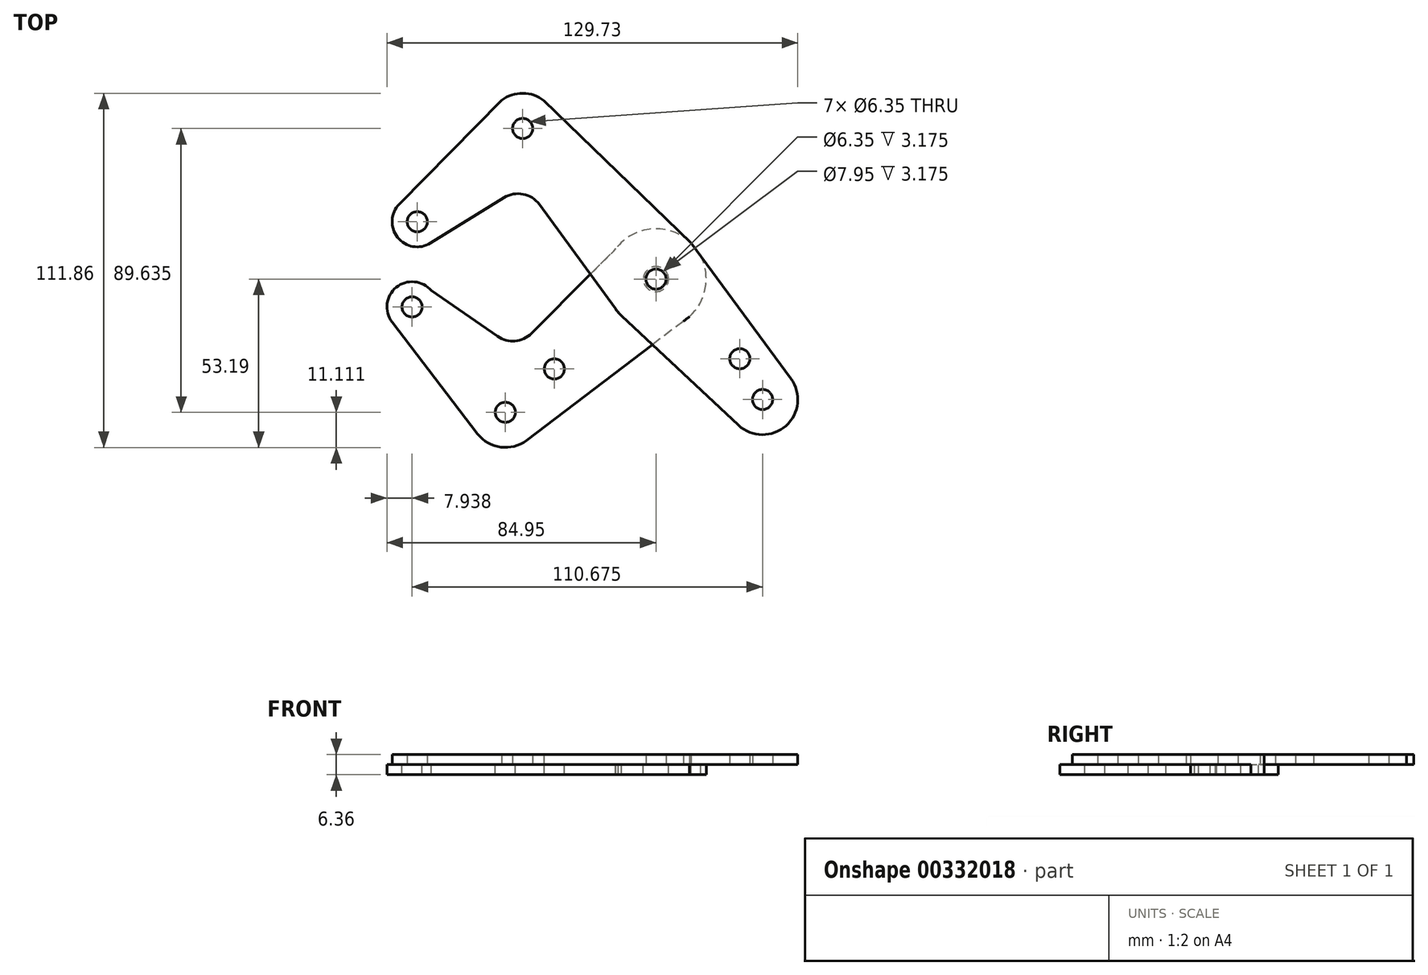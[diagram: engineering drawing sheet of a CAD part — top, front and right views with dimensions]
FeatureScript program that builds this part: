
annotation { "Feature Type Name" : "Feature", "Feature Type Description" : "" }
export const myFeature = defineFeature(function(context is Context, id is Id, definition is map)
    precondition{}
    {
        {
            var Q0;
            Q0=qCreatedBy(makeId("Top.planeOp"),FACE);
            var sketch = newSketch(context, id + "F0", { "sketchPlane" : qUnion([Q0])});
            skCircle(sketch, "E0", {"center": v(0, 0) * mm, "radius": 15.88 * mm});
            skLineSegment(sketch, "E1", {"start": v(-75.37, 18.1) * mm, "end": v(-42.08, 47.56) * mm});
            skLineSegment(sketch, "E2", {"start": v(-42.08, 47.56) * mm, "end": v(0, 0) * mm});
            skLineSegment(sketch, "E3", {"start": v(0, 0) * mm, "end": v(33.66, -38.05) * mm});
            skCircle(sketch, "E4", {"center": v(-75.37, 18.1) * mm, "radius": 7.94 * mm});
            skCircle(sketch, "E5", {"center": v(-42.08, 47.56) * mm, "radius": 11.11 * mm});
            skCircle(sketch, "E6", {"center": v(33.66, -38.05) * mm, "radius": 11.11 * mm});
            skCircle(sketch, "E7", {"center": v(33.66, -38.05) * mm, "radius": 3.18 * mm});
            skCircle(sketch, "E8", {"center": v(0, 0) * mm, "radius": 3.98 * mm});
            skCircle(sketch, "E9", {"center": v(0, 0) * mm, "radius": 3.18 * mm});
            skCircle(sketch, "E10", {"center": v(-75.37, 18.1) * mm, "radius": 3.18 * mm});
            skCircle(sketch, "E11", {"center": v(-42.08, 47.56) * mm, "radius": 3.18 * mm});
            skCircle(sketch, "E12", {"center": v(26.49, -25.15) * mm, "radius": 3.18 * mm});
            skLineSegment(sketch, "E13", {"start": v(0, 0) * mm, "end": v(-47.56, -42.08) * mm});
            skLineSegment(sketch, "E14", {"start": v(-47.56, -42.08) * mm, "end": v(-77.01, -8.79) * mm});
            skLineSegment(sketch, "E15", {"start": v(-81, 23.7) * mm, "end": v(-48.7, 56.48) * mm});
            skLineSegment(sketch, "E16", {"start": v(-35.34, 56.4) * mm, "end": v(11.05, 11.4) * mm});
            skLineSegment(sketch, "E17", {"start": v(11.05, 11.4) * mm, "end": v(42.61, -31.46) * mm});
            skLineSegment(sketch, "E18", {"start": v(26.09, -46.17) * mm, "end": v(-11.94, -10.57) * mm});
            skLineSegment(sketch, "E19", {"start": v(-11.94, -10.57) * mm, "end": v(-36.82, 23.52) * mm});
            skLineSegment(sketch, "E20", {"start": v(-48, 25.7) * mm, "end": v(-71.19, 11.35) * mm});
            skPoint(sketch, "E21.visualSharp", {"position": v(-41.4, 29.8) * mm});
            skArc(sketch, "E21.filletArc", {"start": v(-36.82, 23.52) * mm, "mid": v(-41.99, 26.8) * mm, "end": v(-48, 25.7) * mm});
            skCircle(sketch, "E22", {"center": v(-77.01, -8.79) * mm, "radius": 7.94 * mm});
            skCircle(sketch, "E23", {"center": v(-77.01, -8.79) * mm, "radius": 3.18 * mm});
            skCircle(sketch, "E24", {"center": v(-47.56, -42.08) * mm, "radius": 11.11 * mm});
            skCircle(sketch, "E25", {"center": v(-47.56, -42.08) * mm, "radius": 3.18 * mm});
            skLineSegment(sketch, "E26", {"start": v(-47.56, -42.08) * mm, "end": v(-32.1, -28.4) * mm});
            skCircle(sketch, "E27", {"center": v(-32.1, -28.4) * mm, "radius": 3.18 * mm});
            skLineSegment(sketch, "E28", {"start": v(10.52, -11.89) * mm, "end": v(-40.83, -50.93) * mm});
            skLineSegment(sketch, "E29", {"start": v(-56.34, -48.89) * mm, "end": v(-83.32, -13.61) * mm});
            skLineSegment(sketch, "E30", {"start": v(-70.97, -3.64) * mm, "end": v(-50.01, -18.12) * mm});
            skLineSegment(sketch, "E31", {"start": v(-39.31, -17.14) * mm, "end": v(-12.66, 9.58) * mm});
            skPoint(sketch, "E32.visualSharp", {"position": v(-44.26, -22.1) * mm});
            skArc(sketch, "E32.filletArc", {"start": v(-50.01, -18.12) * mm, "mid": v(-44.49, -19.57) * mm, "end": v(-39.31, -17.14) * mm});
            skSolve(sketch);
        }
        {
            var Q0;
            Q0=makeQuery(id+"F0.imprint","IMPRINT",FACE,{"disambiguationData":[TD([[makeQuery(id+"F0.imprint","IMPRINT",EDGE,{"derivedFrom":sQuery(id+"F0.wireOp",EDGE,"E10")}),-1.0]])]});
            var Q1;
            {var subQ0=sQuery(id+"F0.wireOp",EDGE,"E20");Q1=makeQuery(id+"F0.imprint","IMPRINT",FACE,{"disambiguationData":[TD([[makeQuery(id+"F0.imprint","IMPRINT",EDGE,{"derivedFrom":subQ0}),-1.0]])]});}
            var Q2;
            {var subQ0=sQuery(id+"F0.wireOp",EDGE,"E5");var subQ1=sQuery(id+"F0.wireOp",EDGE,"E1");var subQ2=makeQuery(id+"F0.imprint","INTERSECT",VERTEX,{"derivedFrom":[subQ1,subQ0]});Q2=makeQuery(id+"F0.imprint","IMPRINT",FACE,{"disambiguationData":[TD([[makeQuery(id+"F0.imprint","IMPRINT",EDGE,{"disambiguationData":[TD([[subQ2,-1.0]])],"derivedFrom":subQ1}),-1.0]])]});}
            var Q3;
            {var subQ1=sQuery(id+"F0.wireOp",EDGE,"E5");var subQ3=sQuery(id+"F0.wireOp",EDGE,"E1");var subQ4=makeQuery(id+"F0.imprint","INTERSECT",VERTEX,{"derivedFrom":[subQ3,subQ1]});Q3=makeQuery(id+"F0.imprint","IMPRINT",FACE,{"disambiguationData":[TD([[makeQuery(id+"F0.imprint","IMPRINT",EDGE,{"disambiguationData":[TD([[subQ4,-1.0]])],"derivedFrom":subQ3}),1.0]])]});}
            var Q4;
            {var subQ0=sQuery(id+"F0.wireOp",EDGE,"E4");var subQ1=sQuery(id+"F0.wireOp",EDGE,"E1");var subQ2=makeQuery(id+"F0.imprint","INTERSECT",VERTEX,{"derivedFrom":[subQ1,subQ0]});Q4=makeQuery(id+"F0.imprint","IMPRINT",FACE,{"disambiguationData":[TD([[makeQuery(id+"F0.imprint","IMPRINT",EDGE,{"disambiguationData":[TD([[subQ2,-1.0]])],"derivedFrom":subQ1}),1.0]])]});}
            var Q5;
            {var subQ1=sQuery(id+"F0.wireOp",EDGE,"E0");var subQ3=sQuery(id+"F0.wireOp",EDGE,"E2");var subQ4=makeQuery(id+"F0.imprint","INTERSECT",VERTEX,{"derivedFrom":[subQ1,subQ3]});Q5=makeQuery(id+"F0.imprint","IMPRINT",FACE,{"disambiguationData":[TD([[makeQuery(id+"F0.imprint","IMPRINT",EDGE,{"disambiguationData":[TD([[subQ4,1.0]])],"derivedFrom":subQ3}),1.0]])]});}
            var Q6;
            {var subQ7=sQuery(id+"F0.wireOp",EDGE,"E12");Q6=makeQuery(id+"F0.imprint","IMPRINT",FACE,{"disambiguationData":[TD([[makeQuery(id+"F0.imprint","IMPRINT",EDGE,{"derivedFrom":subQ7}),-1.0]])]});}
            var Q7;
            {var subQ3=sQuery(id+"F0.wireOp",EDGE,"E3");var subQ5=makeQuery(id+"F0.imprint","INTERSECT",VERTEX,{"derivedFrom":[subQ3,sQuery(id+"F0.wireOp",EDGE,"E12")]});Q7=makeQuery(id+"F0.imprint","IMPRINT",FACE,{"disambiguationData":[TD([[makeQuery(id+"F0.imprint","IMPRINT",EDGE,{"disambiguationData":[TD([[subQ5,-1.0]])],"derivedFrom":subQ3}),-1.0]])]});}
            var Q8;
            Q8=makeQuery(id+"F0.imprint","IMPRINT",FACE,{"disambiguationData":[TD([[makeQuery(id+"F0.imprint","IMPRINT",EDGE,{"derivedFrom":sQuery(id+"F0.wireOp",EDGE,"E7")}),-1.0]])]});
            var Q9;
            {var subQ1=sQuery(id+"F0.wireOp",EDGE,"E0");var subQ9=makeQuery(id+"F0.imprint","INTERSECT",VERTEX,{"derivedFrom":[subQ1,sQuery(id+"F0.wireOp",EDGE,"E31")]});Q9=makeQuery(id+"F0.imprint","IMPRINT",FACE,{"disambiguationData":[TD([[makeQuery(id+"F0.imprint","IMPRINT",EDGE,{"disambiguationData":[TD([[subQ9,1.0]])],"derivedFrom":subQ1}),1.0]])]});}
            var Q10;
            {var subQ0=sQuery(id+"F0.wireOp",EDGE,"E31");var subQ1=sQuery(id+"F0.wireOp",EDGE,"E0");var subQ2=makeQuery(id+"F0.imprint","INTERSECT",VERTEX,{"derivedFrom":[subQ1,subQ0]});Q10=makeQuery(id+"F0.imprint","IMPRINT",FACE,{"disambiguationData":[TD([[makeQuery(id+"F0.imprint","IMPRINT",EDGE,{"disambiguationData":[TD([[subQ2,-1.0]])],"derivedFrom":subQ1}),-1.0]])]});}
            var Q11;
            {var subQ0=sQuery(id+"F0.wireOp",EDGE,"E18");var subQ1=sQuery(id+"F0.wireOp",EDGE,"E0");var subQ2=makeQuery(id+"F0.imprint","INTERSECT",VERTEX,{"derivedFrom":[subQ1,subQ0]});Q11=makeQuery(id+"F0.imprint","IMPRINT",FACE,{"disambiguationData":[TD([[makeQuery(id+"F0.imprint","IMPRINT",EDGE,{"disambiguationData":[TD([[subQ2,-1.0]])],"derivedFrom":subQ1}),-1.0]])]});}
            var Q12;
            {var subQ3=sQuery(id+"F0.wireOp",EDGE,"E13");var subQ5=sQuery(id+"F0.wireOp",EDGE,"E0");var subQ6=makeQuery(id+"F0.imprint","INTERSECT",VERTEX,{"derivedFrom":[subQ5,subQ3]});Q12=makeQuery(id+"F0.imprint","IMPRINT",FACE,{"disambiguationData":[TD([[makeQuery(id+"F0.imprint","IMPRINT",EDGE,{"disambiguationData":[TD([[subQ6,-1.0]])],"derivedFrom":subQ5}),1.0]])]});}
            var Q13;
            {var subQ1=sQuery(id+"F0.wireOp",EDGE,"E0");var subQ5=sQuery(id+"F0.wireOp",EDGE,"E2");var subQ6=makeQuery(id+"F0.imprint","INTERSECT",VERTEX,{"derivedFrom":[subQ1,subQ5]});Q13=makeQuery(id+"F0.imprint","IMPRINT",FACE,{"disambiguationData":[TD([[makeQuery(id+"F0.imprint","IMPRINT",EDGE,{"disambiguationData":[TD([[subQ6,-1.0]])],"derivedFrom":subQ5}),1.0]])]});}
            var Q14;
            {var subQ0=sQuery(id+"F0.wireOp",EDGE,"E8");var subQ1=sQuery(id+"F0.wireOp",EDGE,"E2");var subQ2=makeQuery(id+"F0.imprint","INTERSECT",VERTEX,{"derivedFrom":[subQ1,subQ0]});Q14=makeQuery(id+"F0.imprint","IMPRINT",FACE,{"disambiguationData":[TD([[makeQuery(id+"F0.imprint","IMPRINT",EDGE,{"disambiguationData":[TD([[subQ2,-1.0]])],"derivedFrom":subQ1}),1.0]])]});}
            var Q15;
            {var subQ0=sQuery(id+"F0.wireOp",EDGE,"E8");var subQ1=sQuery(id+"F0.wireOp",EDGE,"E2");var subQ2=makeQuery(id+"F0.imprint","INTERSECT",VERTEX,{"derivedFrom":[subQ1,subQ0]});Q15=makeQuery(id+"F0.imprint","IMPRINT",FACE,{"disambiguationData":[TD([[makeQuery(id+"F0.imprint","IMPRINT",EDGE,{"disambiguationData":[TD([[subQ2,-1.0]])],"derivedFrom":subQ1}),-1.0]])]});}
            var Q16;
            {var subQ0=sQuery(id+"F0.wireOp",EDGE,"E9");var subQ1=sQuery(id+"F0.wireOp",EDGE,"E3");var subQ2=makeQuery(id+"F0.imprint","INTERSECT",VERTEX,{"derivedFrom":[subQ1,subQ0]});Q16=makeQuery(id+"F0.imprint","IMPRINT",FACE,{"disambiguationData":[TD([[makeQuery(id+"F0.imprint","IMPRINT",EDGE,{"disambiguationData":[TD([[subQ2,-1.0]])],"derivedFrom":subQ1}),-1.0]])]});}
            extrude(context, id + "F1", {"entities" : qUnion([Q0, Q1, Q2, Q3, Q4, Q5, Q6, Q7, Q8, Q9, Q10, Q11, Q12, Q13, Q14, Q15, Q16]), "depth" : 3.17 * mm});
        }
        {
            var Q0;
            Q0=makeQuery(id+"F0.imprint","IMPRINT",FACE,{"disambiguationData":[TD([[makeQuery(id+"F0.imprint","IMPRINT",EDGE,{"derivedFrom":sQuery(id+"F0.wireOp",EDGE,"E23")}),-1.0]])]});
            var Q1;
            {var subQ4=sQuery(id+"F0.wireOp",EDGE,"E30");Q1=makeQuery(id+"F0.imprint","IMPRINT",FACE,{"disambiguationData":[TD([[makeQuery(id+"F0.imprint","IMPRINT",EDGE,{"derivedFrom":subQ4}),-1.0]])]});}
            var Q2;
            {var subQ0=sQuery(id+"F0.wireOp",EDGE,"E25");var subQ1=sQuery(id+"F0.wireOp",EDGE,"E14");var subQ2=makeQuery(id+"F0.imprint","INTERSECT",VERTEX,{"derivedFrom":[subQ1,subQ0]});Q2=makeQuery(id+"F0.imprint","IMPRINT",FACE,{"disambiguationData":[TD([[makeQuery(id+"F0.imprint","IMPRINT",EDGE,{"disambiguationData":[TD([[subQ2,-1.0]])],"derivedFrom":subQ1}),-1.0]])]});}
            var Q3;
            {var subQ5=sQuery(id+"F0.wireOp",EDGE,"E25");var subQ6=sQuery(id+"F0.wireOp",EDGE,"E14");var subQ7=makeQuery(id+"F0.imprint","INTERSECT",VERTEX,{"derivedFrom":[subQ6,subQ5]});Q3=makeQuery(id+"F0.imprint","IMPRINT",FACE,{"disambiguationData":[TD([[makeQuery(id+"F0.imprint","IMPRINT",EDGE,{"disambiguationData":[TD([[subQ7,-1.0]])],"derivedFrom":subQ6}),1.0]])]});}
            var Q4;
            {var subQ5=sQuery(id+"F0.wireOp",EDGE,"E29");Q4=makeQuery(id+"F0.imprint","IMPRINT",FACE,{"disambiguationData":[TD([[makeQuery(id+"F0.imprint","IMPRINT",EDGE,{"derivedFrom":subQ5}),-1.0]])]});}
            var Q5;
            {var subQ0=sQuery(id+"F0.wireOp",EDGE,"E28");var subQ5=sQuery(id+"F0.wireOp",EDGE,"E18");var subQ6=makeQuery(id+"F0.imprint","INTERSECT",VERTEX,{"derivedFrom":[subQ5,subQ0]});Q5=makeQuery(id+"F0.imprint","IMPRINT",FACE,{"disambiguationData":[TD([[makeQuery(id+"F0.imprint","IMPRINT",EDGE,{"disambiguationData":[TD([[subQ6,-1.0]])],"derivedFrom":subQ5}),1.0]])]});}
            var Q6;
            {var subQ3=sQuery(id+"F0.wireOp",EDGE,"E13");var subQ5=sQuery(id+"F0.wireOp",EDGE,"E0");var subQ6=makeQuery(id+"F0.imprint","INTERSECT",VERTEX,{"derivedFrom":[subQ5,subQ3]});Q6=makeQuery(id+"F0.imprint","IMPRINT",FACE,{"disambiguationData":[TD([[makeQuery(id+"F0.imprint","IMPRINT",EDGE,{"disambiguationData":[TD([[subQ6,-1.0]])],"derivedFrom":subQ5}),1.0]])]});}
            var Q7;
            {var subQ1=sQuery(id+"F0.wireOp",EDGE,"E0");var subQ9=makeQuery(id+"F0.imprint","INTERSECT",VERTEX,{"derivedFrom":[subQ1,sQuery(id+"F0.wireOp",EDGE,"E31")]});Q7=makeQuery(id+"F0.imprint","IMPRINT",FACE,{"disambiguationData":[TD([[makeQuery(id+"F0.imprint","IMPRINT",EDGE,{"disambiguationData":[TD([[subQ9,1.0]])],"derivedFrom":subQ1}),1.0]])]});}
            var Q8;
            {var subQ1=sQuery(id+"F0.wireOp",EDGE,"E0");var subQ5=sQuery(id+"F0.wireOp",EDGE,"E2");var subQ6=makeQuery(id+"F0.imprint","INTERSECT",VERTEX,{"derivedFrom":[subQ1,subQ5]});Q8=makeQuery(id+"F0.imprint","IMPRINT",FACE,{"disambiguationData":[TD([[makeQuery(id+"F0.imprint","IMPRINT",EDGE,{"disambiguationData":[TD([[subQ6,-1.0]])],"derivedFrom":subQ5}),1.0]])]});}
            var Q9;
            {var subQ0=sQuery(id+"F0.wireOp",EDGE,"E31");var subQ1=sQuery(id+"F0.wireOp",EDGE,"E0");var subQ2=makeQuery(id+"F0.imprint","INTERSECT",VERTEX,{"derivedFrom":[subQ1,subQ0]});Q9=makeQuery(id+"F0.imprint","IMPRINT",FACE,{"disambiguationData":[TD([[makeQuery(id+"F0.imprint","IMPRINT",EDGE,{"disambiguationData":[TD([[subQ2,-1.0]])],"derivedFrom":subQ1}),-1.0]])]});}
            var Q10;
            {var subQ0=sQuery(id+"F0.wireOp",EDGE,"E18");var subQ1=sQuery(id+"F0.wireOp",EDGE,"E0");var subQ2=makeQuery(id+"F0.imprint","INTERSECT",VERTEX,{"derivedFrom":[subQ1,subQ0]});Q10=makeQuery(id+"F0.imprint","IMPRINT",FACE,{"disambiguationData":[TD([[makeQuery(id+"F0.imprint","IMPRINT",EDGE,{"disambiguationData":[TD([[subQ2,-1.0]])],"derivedFrom":subQ1}),-1.0]])]});}
            extrude(context, id + "F2", {"entities" : qUnion([Q0, Q1, Q2, Q3, Q4, Q5, Q6, Q7, Q8, Q9, Q10]), "operationType" : NewBodyOperationType.ADD, "oppositeDirection" : true, "depth" : 3.17 * mm});
        }
    });
